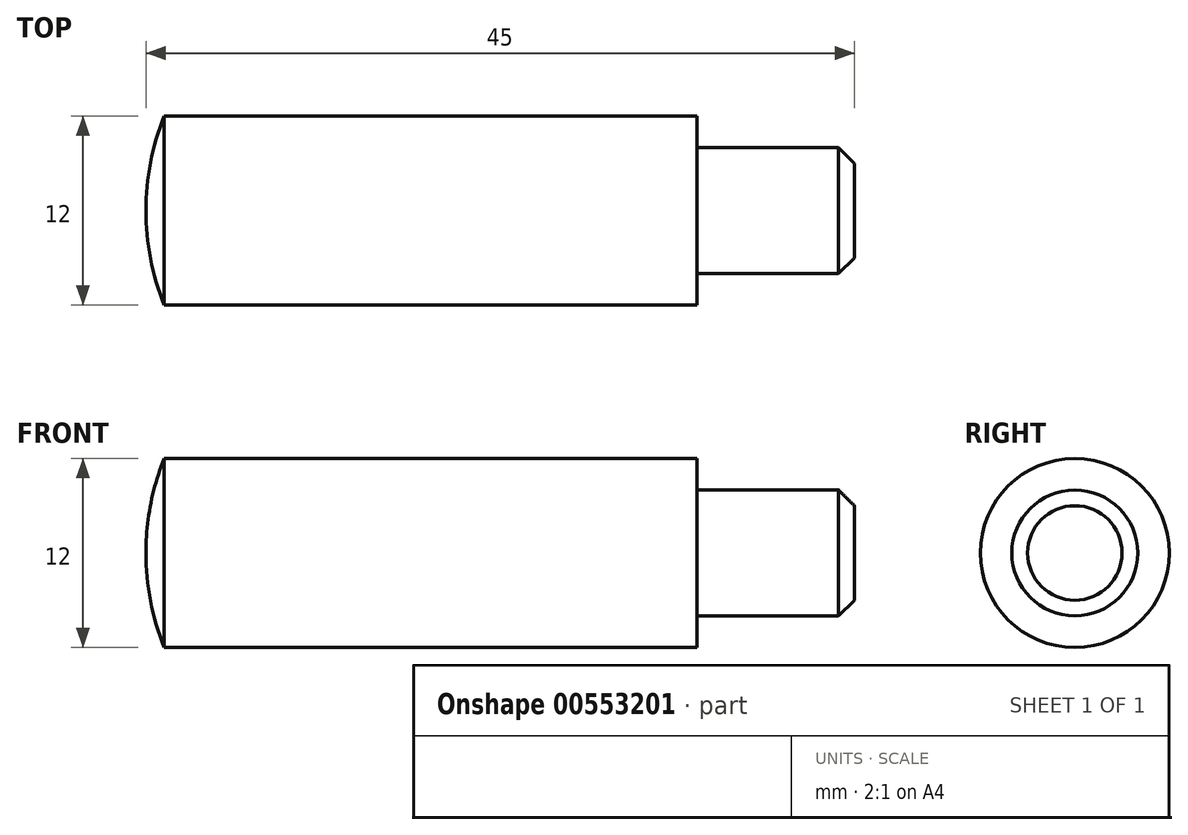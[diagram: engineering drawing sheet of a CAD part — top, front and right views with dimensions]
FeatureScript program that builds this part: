
annotation { "Feature Type Name" : "Feature", "Feature Type Description" : "" }
export const myFeature = defineFeature(function(context is Context, id is Id, definition is map)
    precondition{}
    {
        {
            var Q0;
            Q0=qCreatedBy(makeId("Front.planeOp"),FACE);
            var sketch = newSketch(context, id + "F0", { "sketchPlane" : qUnion([Q0])});
            skLineSegment(sketch, "E0", {"start": v(10, 0) * mm, "end": v(10, 4) * mm});
            skLineSegment(sketch, "E1", {"start": v(10, 4) * mm, "end": v(0, 4) * mm});
            skLineSegment(sketch, "E2", {"start": v(0, 4) * mm, "end": v(0, 6) * mm});
            skLineSegment(sketch, "E3", {"start": v(0, 6) * mm, "end": v(-33.83, 6) * mm});
            skArc(sketch, "E4", {"start": v(-33.83, 6) * mm, "mid": v(-34.7, 3.06) * mm, "end": v(-35, 0) * mm});
            skLineSegment(sketch, "E5", {"start": v(-35, 0) * mm, "end": v(10, 0) * mm});
            skSolve(sketch);
        }
        {
            var Q0;
            Q0 = qSketchRegion(id + "F0", true);
            var Q1;
            Q1=sQuery(id+"F0.wireOp",EDGE,"E5");
            revolve(context, id + "F1", {"entities" : qUnion([Q0]), "axis" : qUnion([Q1]), "revolveType" : RevolveType.FULL});
        }
        {
            var Q0;
            Q0=makeQuery(id+"F1.opRevolve","SWEPT_EDGE",EDGE,{"disambiguationData":[OSD([sQuery(id+"F0.wireOp",EDGE,"E0"),sQuery(id+"F0.wireOp",EDGE,"E1")])]});
            chamfer(context, id + "F2", {"entities" : qUnion([Q0]), "width" : 1 * mm, "tangentPropagation" : true});
        }
    });
